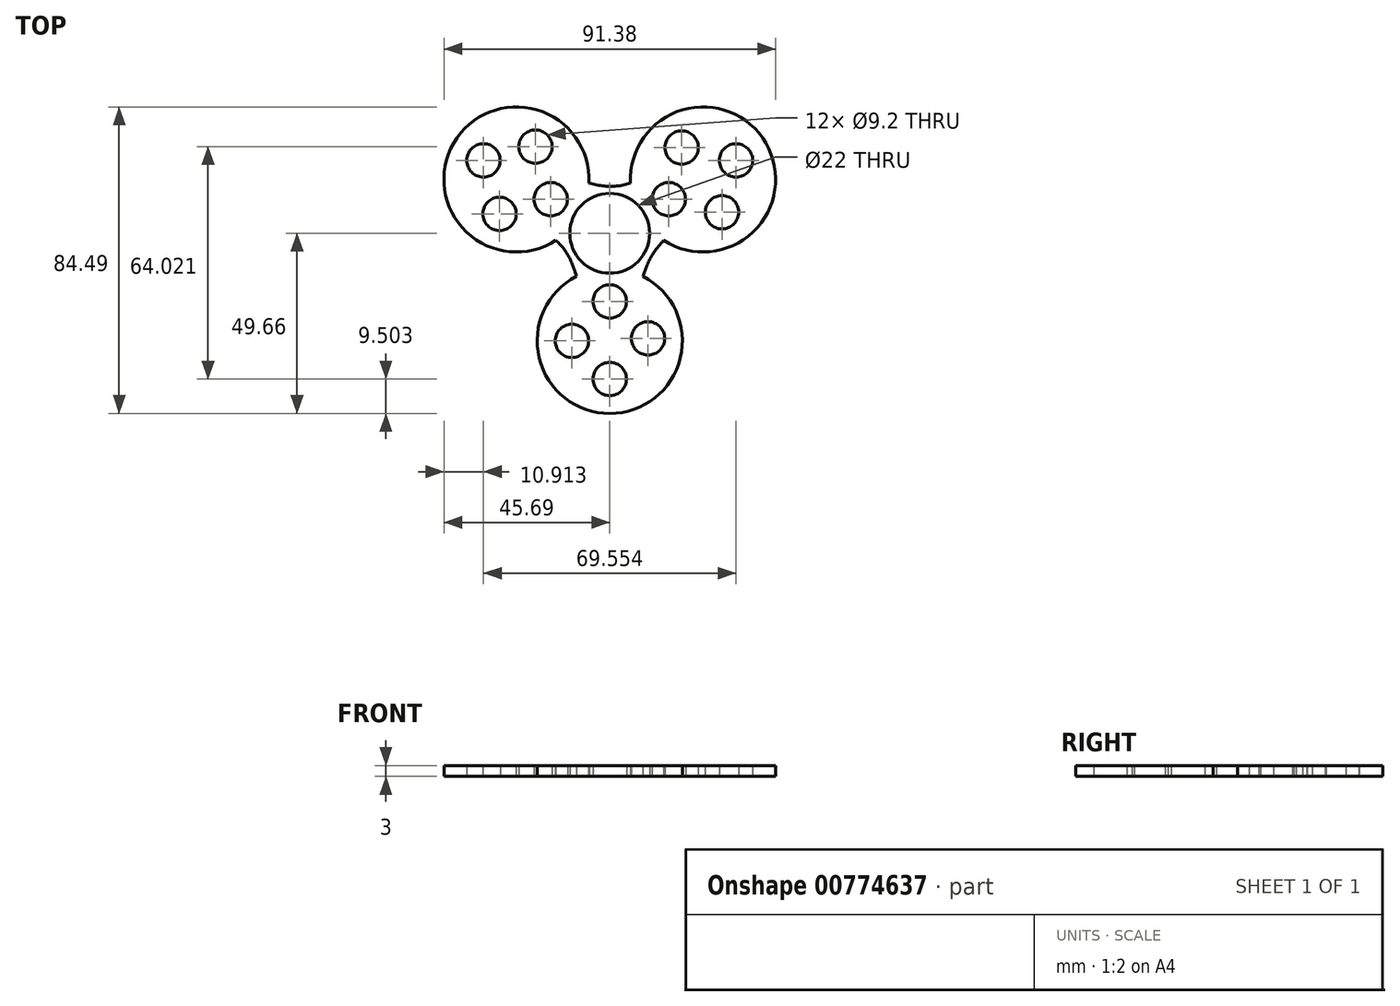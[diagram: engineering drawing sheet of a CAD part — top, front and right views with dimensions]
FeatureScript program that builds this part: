
annotation { "Feature Type Name" : "Feature", "Feature Type Description" : "" }
export const myFeature = defineFeature(function(context is Context, id is Id, definition is map)
    precondition{}
    {
        {
            var Q0;
            Q0=qCreatedBy(makeId("Top.planeOp"),FACE);
            var sketch = newSketch(context, id + "F0", { "sketchPlane" : qUnion([Q0])});
            skCircle(sketch, "E0", {"center": v(0, 0) * mm, "radius": 11 * mm});
            skArc(sketch, "E1", {"start": v(-9.15, -11.88) * mm, "mid": v(0, -49.66) * mm, "end": v(9.15, -11.88) * mm});
            skLineSegment(sketch, "E2", {"start": v(-9.15, -11.88) * mm, "end": v(-9.15, -11.88) * mm});
            skLineSegment(sketch, "E3.MirrorCS", {"start": v(9.15, -11.88) * mm, "end": v(9.15, -11.88) * mm});
            skCircle(sketch, "E4", {"center": v(10.56, -28.97) * mm, "radius": 4.6 * mm});
            skCircle(sketch, "E5", {"center": v(-10.43, -29.66) * mm, "radius": 4.6 * mm});
            skCircle(sketch, "E6", {"center": v(0, -18.77) * mm, "radius": 4.6 * mm});
            skCircle(sketch, "E7.MirrorC", {"center": v(0, -40.16) * mm, "radius": 4.6 * mm});
            skArc(sketch, "E8.1.0", {"start": v(14.87, -1.99) * mm, "mid": v(43.01, 24.83) * mm, "end": v(5.71, 13.87) * mm});
            skCircle(sketch, "E8.1.1", {"center": v(16.26, 9.39) * mm, "radius": 4.6 * mm});
            skCircle(sketch, "E8.1.2", {"center": v(19.8, 23.62) * mm, "radius": 4.6 * mm});
            skCircle(sketch, "E8.1.3", {"center": v(34.78, 20.08) * mm, "radius": 4.6 * mm});
            skCircle(sketch, "E8.1.4", {"center": v(30.9, 5.8) * mm, "radius": 4.6 * mm});
            skArc(sketch, "E8.2.0", {"start": v(-5.71, 13.87) * mm, "mid": v(-43.01, 24.83) * mm, "end": v(-14.87, -1.99) * mm});
            skCircle(sketch, "E8.2.1", {"center": v(-16.26, 9.39) * mm, "radius": 4.6 * mm});
            skCircle(sketch, "E8.2.2", {"center": v(-30.36, 5.34) * mm, "radius": 4.6 * mm});
            skCircle(sketch, "E8.2.3", {"center": v(-34.78, 20.08) * mm, "radius": 4.6 * mm});
            skCircle(sketch, "E8.2.4", {"center": v(-20.48, 23.86) * mm, "radius": 4.6 * mm});
            skFitSpline(sketch, "E9", {"points": [v(-14.87, -1.99) * mm, v(-9.15, -11.88) * mm], "startDerivative": vector(8.53, -7.1) * mm, "endDerivative": vector(4.1, -13.36) * mm});
            skFitSpline(sketch, "E10", {"points": [v(-5.71, 13.87) * mm, v(5.71, 13.87) * mm], "startDerivative": vector(12.8, -3.55) * mm, "endDerivative": vector(11.7, 3.99) * mm});
            skFitSpline(sketch, "E11", {"points": [v(14.87, -1.99) * mm, v(9.15, -11.88) * mm], "startDerivative": vector(-9.23, -9.49) * mm, "endDerivative": vector(-4.28, -12.94) * mm});
            skSolve(sketch);
        }
        {
            var Q0;
            Q0 = qSketchRegion(id + "F0", true);
            extrude(context, id + "F1", {"entities" : qUnion([Q0]), "depth" : 3 * mm, "offsetDistance" : 25 * mm});
        }
    });
